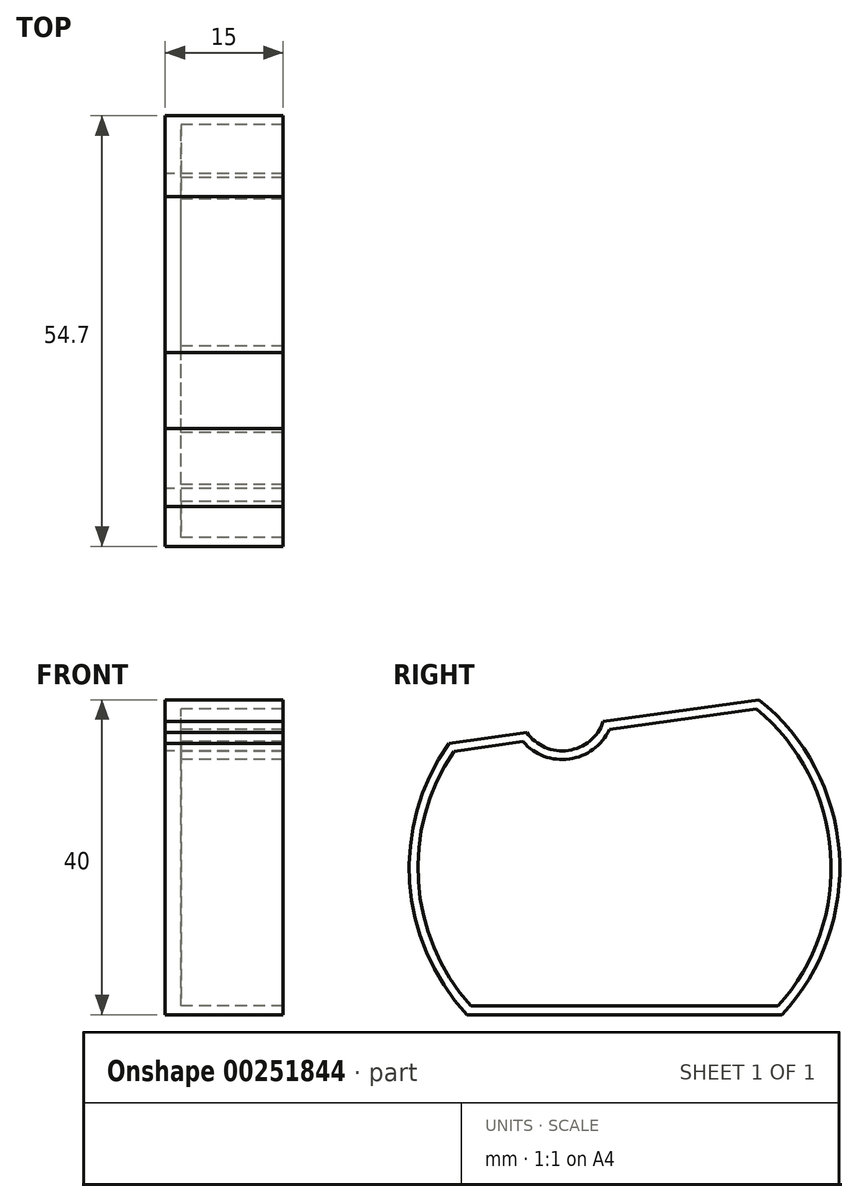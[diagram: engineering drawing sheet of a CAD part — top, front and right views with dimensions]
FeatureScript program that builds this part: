
annotation { "Feature Type Name" : "Feature", "Feature Type Description" : "" }
export const myFeature = defineFeature(function(context is Context, id is Id, definition is map)
    precondition{}
    {
        {
            var Q0;
            Q0=qCreatedBy(makeId("Right.planeOp"),FACE);
            var sketch = newSketch(context, id + "F0", { "sketchPlane" : qUnion([Q0])});
            skArc(sketch, "E0", {"start": v(21.5, -15.89) * mm, "mid": v(28.78, 4.75) * mm, "end": v(18.6, 24.11) * mm});
            skArc(sketch, "E1.trimOffspring", {"start": v(-20.82, 18.58) * mm, "mid": v(-25.79, 0.93) * mm, "end": v(-18.5, -15.89) * mm});
            skLineSegment(sketch, "E2", {"start": v(-20.82, 18.58) * mm, "end": v(-10.91, 19.97) * mm});
            skLineSegment(sketch, "E3.trimOffspring", {"start": v(25.8, -84.09) * mm, "end": v(25.8, -84.09) * mm});
            skLineSegment(sketch, "E4", {"start": v(-18.5, -15.89) * mm, "end": v(21.5, -15.89) * mm});
            skArc(sketch, "E5", {"start": v(-10.91, 19.97) * mm, "mid": v(-5.64, 17.68) * mm, "end": v(-1.21, 21.33) * mm});
            skLineSegment(sketch, "E6.trimOffspring", {"start": v(-1.21, 21.33) * mm, "end": v(18.6, 24.11) * mm});
            skLineSegment(sketch, "E7.0", {"start": v(-20.19, 17.55) * mm, "end": v(-11.39, 18.8) * mm});
            skLineSegment(sketch, "E7.1", {"start": v(-18.02, -14.79) * mm, "end": v(21.02, -14.79) * mm});
            skArc(sketch, "E7.2", {"start": v(21.02, -14.79) * mm, "mid": v(27.68, 4.67) * mm, "end": v(18.27, 22.96) * mm});
            skArc(sketch, "E7.3", {"start": v(-20.19, 17.55) * mm, "mid": v(-24.69, 1) * mm, "end": v(-18.02, -14.79) * mm});
            skLineSegment(sketch, "E7.4", {"start": v(-0.43, 20.33) * mm, "end": v(18.27, 22.96) * mm});
            skArc(sketch, "E7.5", {"start": v(-11.39, 18.8) * mm, "mid": v(-5.5, 16.59) * mm, "end": v(-0.43, 20.33) * mm});
            skSolve(sketch);
        }
        {
            var Q0;
            Q0=makeQuery(id+"F0.imprint","IMPRINT",FACE,{"disambiguationData":[TD([[makeQuery(id+"F0.imprint","IMPRINT",EDGE,{"derivedFrom":sQuery(id+"F0.wireOp",EDGE,"E0")}),1.0]])]});
            extrude(context, id + "F1", {"entities" : qUnion([Q0]), "depth" : 15 * mm});
        }
        {
            var Q0;
            Q0=makeQuery(id+"F0.imprint","IMPRINT",FACE,{"disambiguationData":[TD([[makeQuery(id+"F0.imprint","IMPRINT",EDGE,{"derivedFrom":sQuery(id+"F0.wireOp",EDGE,"E7.0")}),-1.0]])]});
            extrude(context, id + "F2", {"entities" : qUnion([Q0]), "operationType" : NewBodyOperationType.ADD, "depth" : 2 * mm});
        }
    });
